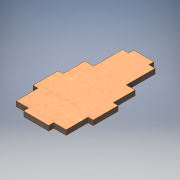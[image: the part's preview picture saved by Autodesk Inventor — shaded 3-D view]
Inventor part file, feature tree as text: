
AUTODESK INVENTOR PART (.ipt)
format: ipt  version: 2019 (Build 230136000, 136)  size: 142,336 bytes
history: native  units: mm
features: other x1, extrude x1, sketch x1
ambient origin geometry x8: Origin, YZ Plane, XZ Plane, XY Plane, X Axis, Y Axis, Z Axis, Center Point
bodies: Body1 (feature_tree)
feature tree (3):
  other  "Твердое тело1"
  extrude  "Выдавливание1"  Depth=16.0mm
  sketch  "Эскиз1"
